# Revit family: M_Ceiling Light - Linear Box
name_source: partatom
category: Lighting Fixtures
revit_build: Autodesk Revit 2017 (Build: 20160109_1515(x64)
units: mm (PartAtom-declared; Revit-internal decimal feet)

## family parameters
Always vertical = No
Cut with Voids When Loaded = No
Host = Ceiling
Light Source = Yes
OmniClass Number = 23.80.70.11.11
OmniClass Title = General Luminaries, Non Directional
Part Type = Normal
Room Calculation Point = No
Round Connector Dimension = Use Diameter
Shared = No

## types (8) — shared parameters
Assembly Code = D5020210
Ballast Number of Poles = 1
Color Filter = 16777215
Diffuser Material = Glass, White, High Luminance
Dimming Lamp Color Temperature Shift = <None>
Emit Shape Visible in Rendering = No
Lamp = T-12
Light Box Material = Steel, Paint Finish, Ivory, Glossy
Light Source Symbol Size = 610 mm
Load Classification = Lighting - Dwelling Unit

## per-type parameters (varying)
| type | Apparent Load | Ballast Voltage | Box Length | Box Width | Emit from Rectangle Length | Emit from Rectangle Width |
| 0300x1200mm(1 Lamp) - 120V | 40 VA | 120 V | 1200 mm  [stored 3.93701 ft] | 300 mm | 1174 mm  [stored 3.85171 ft] | 274 mm  [stored 0.89895 ft] |
| 0300x1200mm(1 Lamp) - 277V | 40 VA | 277 V | 1200 mm  [stored 3.93701 ft] | 300 mm | 1174 mm  [stored 3.85171 ft] | 274 mm  [stored 0.89895 ft] |
| 0300x1200mm(2 Lamp) - 120V | 80 VA | 120 V | 1200 mm  [stored 3.93701 ft] | 300 mm | 1174 mm  [stored 3.85171 ft] | 274 mm  [stored 0.89895 ft] |
| 0300x1200mm(2 Lamp) - 277V | 80 VA | 120 V | 1200 mm  [stored 3.93701 ft] | 300 mm | 1174 mm  [stored 3.85171 ft] | 274 mm  [stored 0.89895 ft] |
| 0600x0600mm(2 Lamp) - 120V | 40 VA | 120 V | 600 mm  [stored 1.9685 ft] | 600 mm  [stored 1.9685 ft] | 574 mm | 574 mm |
| 0600x0600mm(2 Lamp) - 277V | 40 VA | 120 V | 600 mm  [stored 1.9685 ft] | 600 mm  [stored 1.9685 ft] | 574 mm | 574 mm |
| 0600x1200mm(2 Lamp) - 120V | 80 VA | 120 V | 1200 mm  [stored 3.93701 ft] | 600 mm  [stored 1.9685 ft] | 1174 mm  [stored 3.85171 ft] | 574 mm |
| 0600x1200mm(2 Lamp) - 277V | 80 VA | 277 V | 1200 mm  [stored 3.93701 ft] | 600 mm  [stored 1.9685 ft] | 1174 mm  [stored 3.85171 ft] | 574 mm |

note: [stored X ft] marks values corroborated as IEEE doubles in the binary element streams (Revit-internal decimal feet)

## geometry (parser evidence)
native form markers: Sweep x1
no freeform markers — native parametric forms only
